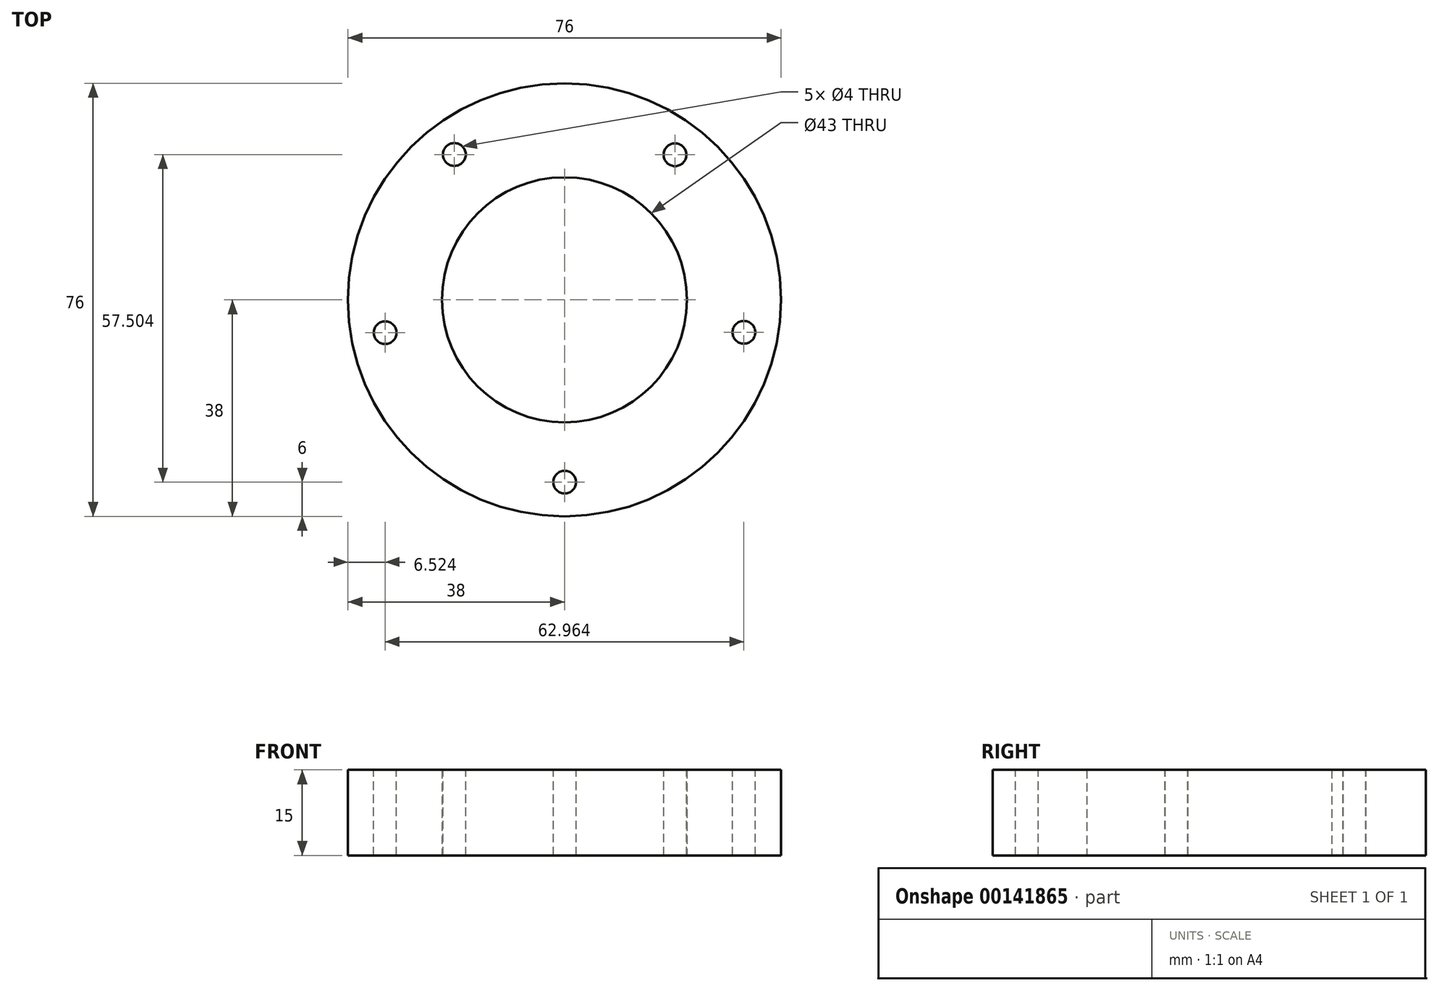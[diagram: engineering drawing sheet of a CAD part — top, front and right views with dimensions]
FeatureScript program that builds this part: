
annotation { "Feature Type Name" : "Feature", "Feature Type Description" : "" }
export const myFeature = defineFeature(function(context is Context, id is Id, definition is map)
    precondition{}
    {
        {
            var Q0;
            Q0=qCreatedBy(makeId("Top.planeOp"),FACE);
            var sketch = newSketch(context, id + "F0", { "sketchPlane" : qUnion([Q0])});
            skCircle(sketch, "E0", {"center": v(0, 0) * mm, "radius": 38 * mm});
            skCircle(sketch, "E1", {"center": v(0, 0) * mm, "radius": 21.5 * mm});
            skSolve(sketch);
        }
        {
            var Q0;
            Q0=qSketchRegion(id+"F0",true);
            extrude(context, id + "F1", {"entities" : qUnion([Q0]), "depth" : 10 * mm});
        }
        {
            var Q0;
            Q0=makeQuery(id+"F1.opExtrude","CAP_FACE",FACE,{"disambiguationData":[OSD([sQuery(id+"F0.wireOp",EDGE,"E0"),sQuery(id+"F0.wireOp",EDGE,"E1")])],"isStart":false});
            var sketch = newSketch(context, id + "F2", { "sketchPlane" : qUnion([Q0])});
            skCircle(sketch, "E2", {"center": v(0, 0) * mm, "radius": 32 * mm});
            skCircle(sketch, "E3", {"center": v(-19.33, 25.5) * mm, "radius": 2 * mm});
            skCircle(sketch, "E4", {"center": v(19.4, 25.45) * mm, "radius": 2 * mm});
            skLineSegment(sketch, "E5", {"start": v(-17.33, 25.5) * mm, "end": v(17.4, 25.5) * mm});
            skLineSegment(sketch, "E6", {"start": v(0.03, 25.5) * mm, "end": v(0.03, -32) * mm});
            skCircle(sketch, "E7", {"center": v(0.03, -32) * mm, "radius": 2 * mm});
            skLineSegment(sketch, "E8", {"start": v(0.03, -32) * mm, "end": v(31.49, -5.7) * mm});
            skLineSegment(sketch, "E9", {"start": v(0.03, -32) * mm, "end": v(-31.48, -5.77) * mm});
            skCircle(sketch, "E10", {"center": v(-31.48, -5.77) * mm, "radius": 2 * mm});
            skCircle(sketch, "E11", {"center": v(31.49, -5.7) * mm, "radius": 2 * mm});
            skSolve(sketch);
        }
        {
            var Q0;
            {var subQ0=sQuery(id+"F2.wireOp",EDGE,"E3");var subQ1=sQuery(id+"F2.wireOp",EDGE,"E2");var subQ2=makeQuery(id+"F2.imprint","INTERSECT",VERTEX,{"disambiguationData":[OD(0.0)],"derivedFrom":[subQ1,subQ0]});Q0=makeQuery(id+"F2.imprint","IMPRINT",FACE,{"disambiguationData":[TD([[makeQuery(id+"F2.imprint","IMPRINT",EDGE,{"disambiguationData":[TD([[subQ2,-1.0]])],"derivedFrom":subQ1}),1.0]])]});}
            var Q1;
            {var subQ0=sQuery(id+"F2.wireOp",EDGE,"E3");var subQ1=sQuery(id+"F2.wireOp",EDGE,"E2");var subQ2=makeQuery(id+"F2.imprint","INTERSECT",VERTEX,{"disambiguationData":[OD(0.0)],"derivedFrom":[subQ1,subQ0]});Q1=makeQuery(id+"F2.imprint","IMPRINT",FACE,{"disambiguationData":[TD([[makeQuery(id+"F2.imprint","IMPRINT",EDGE,{"disambiguationData":[TD([[subQ2,-1.0]])],"derivedFrom":subQ1}),-1.0]])]});}
            var Q2;
            {var subQ0=sQuery(id+"F2.wireOp",EDGE,"E4");var subQ1=sQuery(id+"F2.wireOp",EDGE,"E2");var subQ2=makeQuery(id+"F2.imprint","INTERSECT",VERTEX,{"disambiguationData":[OD(0.0)],"derivedFrom":[subQ1,subQ0]});Q2=makeQuery(id+"F2.imprint","IMPRINT",FACE,{"disambiguationData":[TD([[makeQuery(id+"F2.imprint","IMPRINT",EDGE,{"disambiguationData":[TD([[subQ2,1.0]])],"derivedFrom":subQ1}),1.0]])]});}
            var Q3;
            {var subQ0=sQuery(id+"F2.wireOp",EDGE,"E4");var subQ1=sQuery(id+"F2.wireOp",EDGE,"E2");var subQ2=makeQuery(id+"F2.imprint","INTERSECT",VERTEX,{"disambiguationData":[OD(0.0)],"derivedFrom":[subQ1,subQ0]});Q3=makeQuery(id+"F2.imprint","IMPRINT",FACE,{"disambiguationData":[TD([[makeQuery(id+"F2.imprint","IMPRINT",EDGE,{"disambiguationData":[TD([[subQ2,1.0]])],"derivedFrom":subQ1}),-1.0]])]});}
            var Q4;
            {var subQ0=sQuery(id+"F2.wireOp",EDGE,"E2");var subQ1=makeQuery(id+"F2.imprint","INTERSECT",VERTEX,{"derivedFrom":[subQ0,sQuery(id+"F2.wireOp",EDGE,"E6")]});Q4=makeQuery(id+"F2.imprint","IMPRINT",FACE,{"disambiguationData":[TD([[makeQuery(id+"F2.imprint","IMPRINT",EDGE,{"disambiguationData":[TD([[subQ1,1.0]])],"derivedFrom":subQ0}),-1.0]])]});}
            var Q5;
            {var subQ0=sQuery(id+"F2.wireOp",EDGE,"E6");var subQ1=sQuery(id+"F2.wireOp",EDGE,"E2");var subQ2=makeQuery(id+"F2.imprint","INTERSECT",VERTEX,{"derivedFrom":[subQ1,subQ0]});Q5=makeQuery(id+"F2.imprint","IMPRINT",FACE,{"disambiguationData":[TD([[makeQuery(id+"F2.imprint","IMPRINT",EDGE,{"disambiguationData":[TD([[subQ2,1.0]])],"derivedFrom":subQ1}),1.0]])]});}
            var Q6;
            {var subQ0=sQuery(id+"F2.wireOp",EDGE,"E6");var subQ1=sQuery(id+"F2.wireOp",EDGE,"E2");var subQ2=makeQuery(id+"F2.imprint","INTERSECT",VERTEX,{"derivedFrom":[subQ1,subQ0]});Q6=makeQuery(id+"F2.imprint","IMPRINT",FACE,{"disambiguationData":[TD([[makeQuery(id+"F2.imprint","IMPRINT",EDGE,{"disambiguationData":[TD([[subQ2,-1.0]])],"derivedFrom":subQ1}),1.0]])]});}
            var Q7;
            {var subQ1=sQuery(id+"F2.wireOp",EDGE,"E6");var subQ3=sQuery(id+"F2.wireOp",EDGE,"E7");var subQ4=makeQuery(id+"F2.imprint","INTERSECT",VERTEX,{"derivedFrom":[subQ1,subQ3]});Q7=makeQuery(id+"F2.imprint","IMPRINT",FACE,{"disambiguationData":[TD([[makeQuery(id+"F2.imprint","IMPRINT",EDGE,{"disambiguationData":[TD([[subQ4,-1.0]])],"derivedFrom":subQ3}),1.0]])]});}
            var Q8;
            {var subQ1=sQuery(id+"F2.wireOp",EDGE,"E6");var subQ3=sQuery(id+"F2.wireOp",EDGE,"E7");var subQ4=makeQuery(id+"F2.imprint","INTERSECT",VERTEX,{"derivedFrom":[subQ1,subQ3]});Q8=makeQuery(id+"F2.imprint","IMPRINT",FACE,{"disambiguationData":[TD([[makeQuery(id+"F2.imprint","IMPRINT",EDGE,{"disambiguationData":[TD([[subQ4,1.0]])],"derivedFrom":subQ3}),1.0]])]});}
            var Q9;
            {var subQ0=sQuery(id+"F2.wireOp",EDGE,"E8");var subQ1=sQuery(id+"F2.wireOp",EDGE,"E2");var subQ2=makeQuery(id+"F2.imprint","INTERSECT",VERTEX,{"derivedFrom":[subQ1,subQ0]});Q9=makeQuery(id+"F2.imprint","IMPRINT",FACE,{"disambiguationData":[TD([[makeQuery(id+"F2.imprint","IMPRINT",EDGE,{"disambiguationData":[TD([[subQ2,-1.0]])],"derivedFrom":subQ1}),1.0]])]});}
            var Q10;
            {var subQ0=sQuery(id+"F2.wireOp",EDGE,"E2");var subQ1=makeQuery(id+"F2.imprint","INTERSECT",VERTEX,{"derivedFrom":[subQ0,sQuery(id+"F2.wireOp",EDGE,"E8")]});Q10=makeQuery(id+"F2.imprint","IMPRINT",FACE,{"disambiguationData":[TD([[makeQuery(id+"F2.imprint","IMPRINT",EDGE,{"disambiguationData":[TD([[subQ1,1.0]])],"derivedFrom":subQ0}),-1.0]])]});}
            var Q11;
            {var subQ0=sQuery(id+"F2.wireOp",EDGE,"E8");var subQ1=sQuery(id+"F2.wireOp",EDGE,"E2");var subQ2=makeQuery(id+"F2.imprint","INTERSECT",VERTEX,{"derivedFrom":[subQ1,subQ0]});Q11=makeQuery(id+"F2.imprint","IMPRINT",FACE,{"disambiguationData":[TD([[makeQuery(id+"F2.imprint","IMPRINT",EDGE,{"disambiguationData":[TD([[subQ2,1.0]])],"derivedFrom":subQ1}),1.0]])]});}
            var Q12;
            {var subQ0=sQuery(id+"F2.wireOp",EDGE,"E2");var subQ1=makeQuery(id+"F2.imprint","INTERSECT",VERTEX,{"derivedFrom":[subQ0,sQuery(id+"F2.wireOp",EDGE,"E9")]});Q12=makeQuery(id+"F2.imprint","IMPRINT",FACE,{"disambiguationData":[TD([[makeQuery(id+"F2.imprint","IMPRINT",EDGE,{"disambiguationData":[TD([[subQ1,1.0]])],"derivedFrom":subQ0}),-1.0]])]});}
            var Q13;
            {var subQ0=sQuery(id+"F2.wireOp",EDGE,"E9");var subQ1=sQuery(id+"F2.wireOp",EDGE,"E2");var subQ2=makeQuery(id+"F2.imprint","INTERSECT",VERTEX,{"derivedFrom":[subQ1,subQ0]});Q13=makeQuery(id+"F2.imprint","IMPRINT",FACE,{"disambiguationData":[TD([[makeQuery(id+"F2.imprint","IMPRINT",EDGE,{"disambiguationData":[TD([[subQ2,1.0]])],"derivedFrom":subQ1}),1.0]])]});}
            var Q14;
            {var subQ0=sQuery(id+"F2.wireOp",EDGE,"E9");var subQ1=sQuery(id+"F2.wireOp",EDGE,"E2");var subQ2=makeQuery(id+"F2.imprint","INTERSECT",VERTEX,{"derivedFrom":[subQ1,subQ0]});Q14=makeQuery(id+"F2.imprint","IMPRINT",FACE,{"disambiguationData":[TD([[makeQuery(id+"F2.imprint","IMPRINT",EDGE,{"disambiguationData":[TD([[subQ2,-1.0]])],"derivedFrom":subQ1}),1.0]])]});}
            extrude(context, id + "F3", {"entities" : qUnion([Q0, Q1, Q2, Q3, Q4, Q5, Q6, Q7, Q8, Q9, Q10, Q11, Q12, Q13, Q14]), "operationType" : NewBodyOperationType.REMOVE, "oppositeDirection" : true, "depth" : 10 * mm});
        }
        {
            var Q0;
            Q0=makeQuery(id+"F1.opExtrude","CAP_FACE",FACE,{"disambiguationData":[OSD([sQuery(id+"F0.wireOp",EDGE,"E0"),sQuery(id+"F0.wireOp",EDGE,"E1")])],"isStart":false});
            extrude(context, id + "F4", {"entities" : qUnion([Q0]), "operationType" : NewBodyOperationType.ADD, "depth" : 5 * mm});
        }
    });
